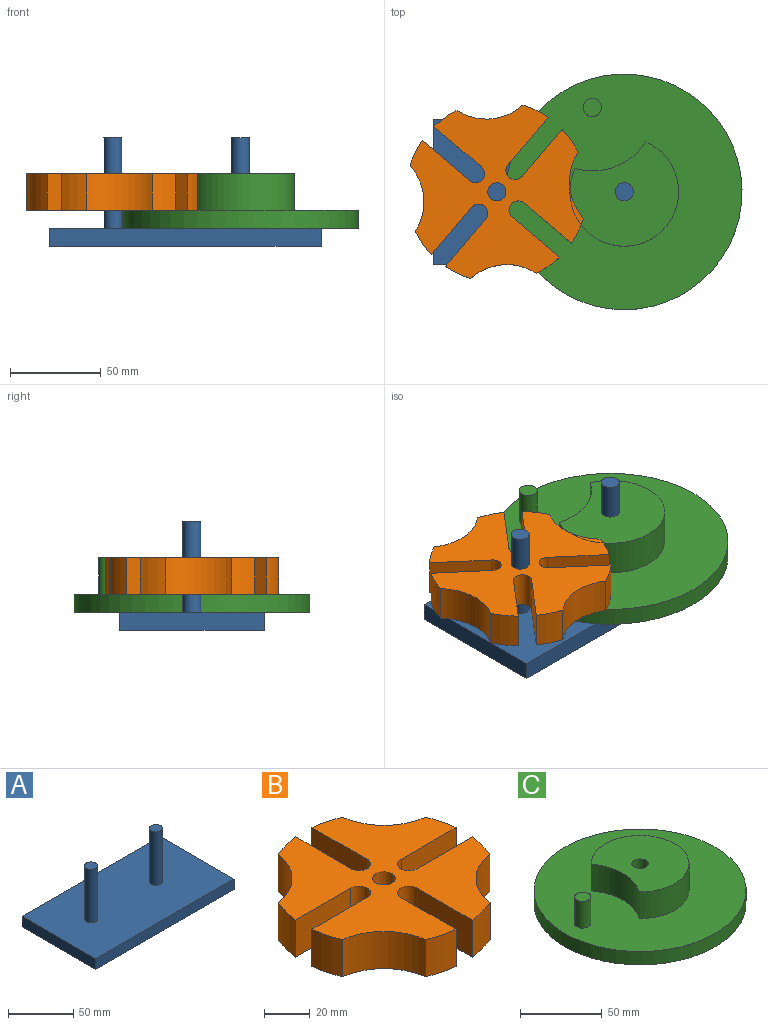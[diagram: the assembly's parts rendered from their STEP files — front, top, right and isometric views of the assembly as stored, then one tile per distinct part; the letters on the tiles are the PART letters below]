
ASSEMBLY  parts=3 mates=4
PART A: 10 faces, bbox 150x80x60 mm
  f0: plane 150x10mm, normal (0,1,0), area 1500mm2, adj f1,f3,f4,f5
  f1: plane 80x10mm, normal (-1,0,0), area 800mm2, adj f0,f2,f4,f5
  f2: plane 150x10mm, normal (0,-1,0), area 1500mm2, adj f1,f3,f4,f5
  f3: plane 80x10mm, normal (1,0,0), area 800mm2, adj f0,f2,f4,f5
  f4: plane 150x80mm, normal (0,0,1), area 11842.9mm2, adj f0,f1,f2,f3,f6,f8
  f5: plane 150x80mm, normal (0,0,-1), area 12000mm2, adj f0,f1,f2,f3
  f6: cylinder r=5mm len=50mm, axis (0,0,-1), area 1570.8mm2, adj f4,f7
  f7: plane 10x10mm, normal (0,0,1), area 78.5mm2, adj f6
  f8: cylinder r=5mm len=50mm, axis (0,0,-1), area 1570.8mm2, adj f4,f9
  f9: plane 10x10mm, normal (0,0,1), area 78.5mm2, adj f8
PART B: 27 faces, bbox 99.5x99.5x20 mm
  f0: cylinder r=30mm len=25.81mm, axis (0,0,-1), area 784.9mm2, adj f1,f24,f25,f26
  f1: cylinder r=50mm len=20mm, axis (0,0,-1), area 311.5mm2, adj f0,f2,f25,f26
  f2: plane 34.23x20mm, normal (0,-1,0), area 684.6mm2, adj f1,f3,f25,f26
  f3: cylinder r=5mm len=20mm, axis (0,0,-1), area 319.5mm2, adj f2,f4,f25,f26
  f4: plane 34.11x20mm, normal (0,1,0), area 682.2mm2, adj f3,f5,f25,f26
  f5: cylinder r=50mm len=20mm, axis (0,0,-1), area 311.6mm2, adj f4,f6,f25,f26
  f6: cylinder r=30mm len=25.81mm, axis (0,0,-1), area 784.9mm2, adj f5,f7,f25,f26
  f7: cylinder r=50mm len=20mm, axis (0,0,-1), area 311.5mm2, adj f6,f8,f25,f26
  f8: plane 34.23x20mm, normal (1,0,0), area 684.6mm2, adj f7,f9,f25,f26
  f9: cylinder r=5mm len=20mm, axis (0,0,-1), area 319.5mm2, adj f8,f10,f25,f26
  f10: plane 34.11x20mm, normal (-1,0,0), area 682.2mm2, adj f9,f11,f25,f26
  f11: cylinder r=50mm len=20mm, axis (0,0,-1), area 311.6mm2, adj f10,f12,f25,f26
  f12: cylinder r=30mm len=25.81mm, axis (0,0,-1), area 784.9mm2, adj f11,f13,f25,f26
  f13: cylinder r=50mm len=20mm, axis (0,0,-1), area 311.5mm2, adj f12,f14,f25,f26
  f14: plane 34.23x20mm, normal (0,1,0), area 684.6mm2, adj f13,f15,f25,f26
  f15: cylinder r=5mm len=20mm, axis (0,0,-1), area 319.5mm2, adj f14,f16,f25,f26
  f16: plane 34.11x20mm, normal (0,-1,0), area 682.2mm2, adj f15,f17,f25,f26
  f17: cylinder r=50mm len=20mm, axis (0,0,-1), area 311.6mm2, adj f16,f18,f25,f26
  f18: cylinder r=30mm len=25.81mm, axis (0,0,-1), area 784.9mm2, adj f17,f19,f25,f26
  f19: cylinder r=50mm len=20mm, axis (0,0,-1), area 311.5mm2, adj f18,f20,f25,f26
  f20: plane 34.23x20mm, normal (-1,0,0), area 684.6mm2, adj f19,f21,f25,f26
  f21: cylinder r=5mm len=20mm, axis (0,0,-1), area 319.5mm2, adj f20,f22,f25,f26
  f22: plane 34.11x20mm, normal (1,0,0), area 682.2mm2, adj f21,f24,f25,f26
  f23: cylinder r=5mm len=20mm, axis (0,0,-1), area 628.3mm2, adj f25,f26
  f24: cylinder r=50mm len=20mm, axis (0,0,-1), area 311.6mm2, adj f0,f22,f25,f26
  f25: plane 99.5x99.5mm, normal (0,0,1), area 5285.3mm2, adj f0,f1,f2,f3,f4,f5,f6,f7
  f26: plane 99.5x99.5mm, normal (0,0,-1), area 5285.3mm2, adj f0,f1,f2,f3,f4,f5,f6,f7
PART C: 9 faces, bbox 130x130x30 mm
  f0: plane 130x130mm, normal (0,0,1), area 10801.9mm2, adj f1,f3,f4,f6
  f1: cylinder r=65mm len=130mm, axis (0,0,-1), area 4084.1mm2, adj f0,f2
  f2: plane 130x130mm, normal (0,0,-1), area 13194.7mm2, adj f1,f8
  f3: cylinder r=35mm len=41.62mm, axis (0,0,-1), area 891.4mm2, adj f0,f4,f5
  f4: cylinder r=30mm len=60mm, axis (0,0,-1), area 2850mm2, adj f0,f3,f5
  f5: plane 60x51.61mm, normal (0,0,1), area 2314.3mm2, adj f3,f4,f8
  f6: cylinder r=5mm len=20mm, axis (0,0,-1), area 628.3mm2, adj f0,f7
  f7: plane 10x10mm, normal (0,0,1), area 78.5mm2, adj f6
  f8: cylinder r=5mm len=30mm, axis (0,0,1), area 942.5mm2, adj f2,f5
PLACE A t=(97.37,-102.23,-105.65)mm fixed
PLACE B rot(axis=(-0.94,0.35,0),180deg) t=(66.2,-108.49,-65.65)mm
PLACE C rot(axis=(0,0,-1),69.3deg) t=(136.56,-108.49,-95.65)mm
MATE revolute A.f8 <-> C.f4  axis (0,0,1) through (136.56,-108.49,-70.65)mm
MATE planar B.f24 <-> A.f6  axis (0,0,-1) through (66.2,-108.49,-85.65)mm
MATE planar C.f8 <-> A.f8  axis (0,0,-1) through (136.56,-108.49,-95.65)mm
MATE revolute A.f6 <-> B.f1  axis (0,0,-1) through (66.2,-108.49,-70.65)mm
